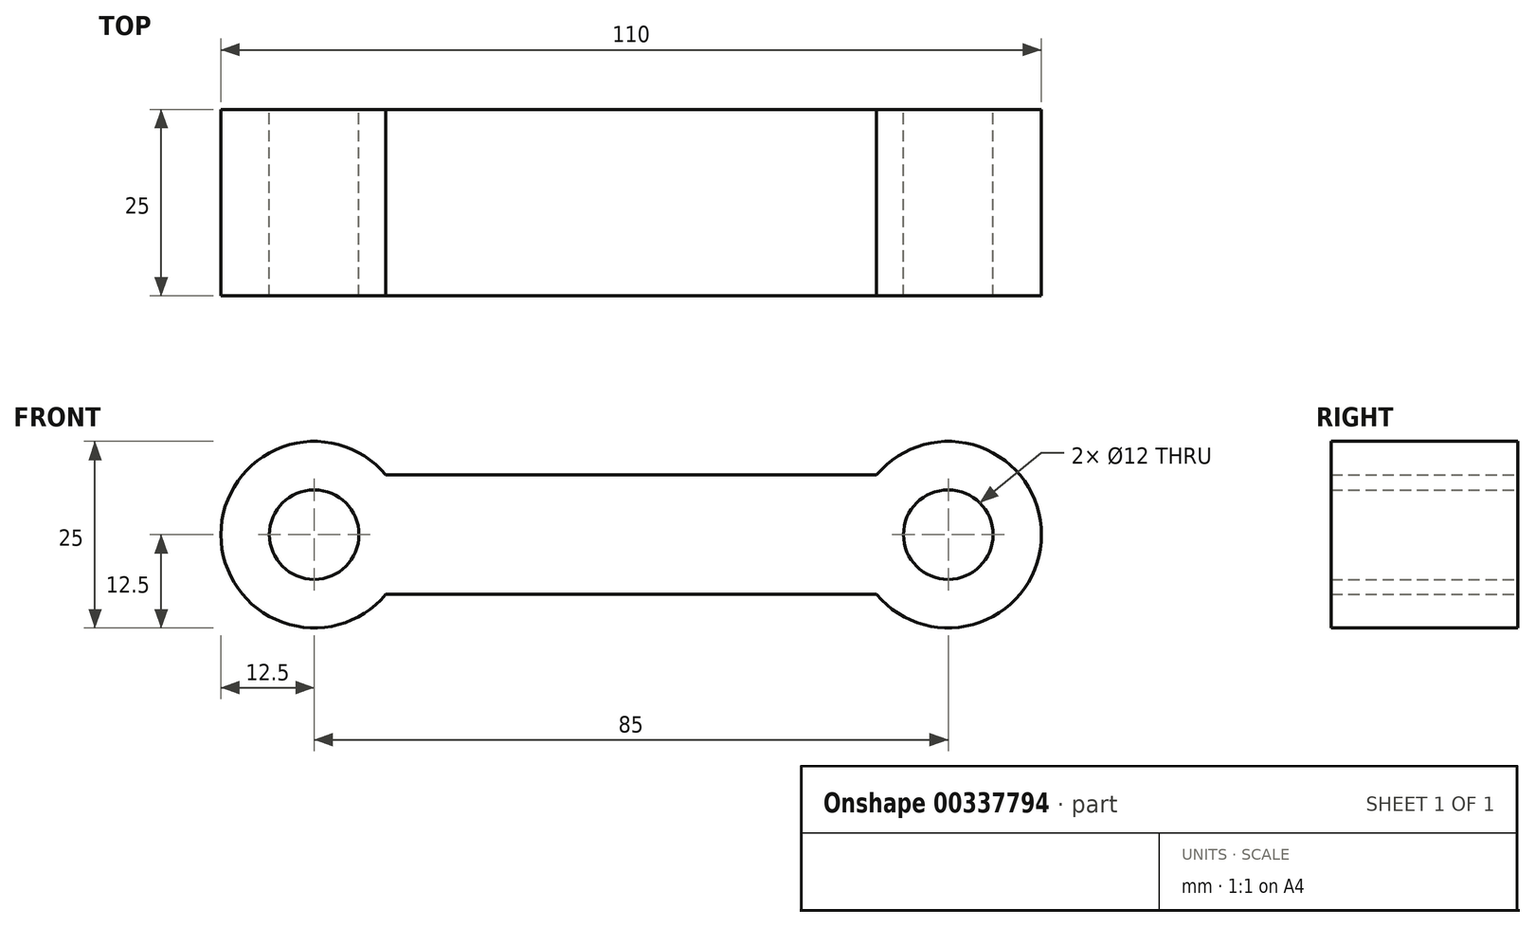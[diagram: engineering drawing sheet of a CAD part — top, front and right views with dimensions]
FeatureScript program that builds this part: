
annotation { "Feature Type Name" : "Feature", "Feature Type Description" : "" }
export const myFeature = defineFeature(function(context is Context, id is Id, definition is map)
    precondition{}
    {
        {
            var Q0;
            Q0=qCreatedBy(makeId("Front.planeOp"),FACE);
            var sketch = newSketch(context, id + "F0", { "sketchPlane" : qUnion([Q0])});
            skCircle(sketch, "E0", {"center": v(0, 0) * mm, "radius": 12.5 * mm});
            skCircle(sketch, "E1", {"center": v(85, 0) * mm, "radius": 12.5 * mm});
            skLineSegment(sketch, "E2", {"start": v(9.6, 8) * mm, "end": v(75.4, 8) * mm});
            skLineSegment(sketch, "E3", {"start": v(0, 0) * mm, "end": v(85, 0) * mm, "construction": true});
            skLineSegment(sketch, "E4.MirrorCS", {"start": v(9.6, -8) * mm, "end": v(75.4, -8) * mm});
            skCircle(sketch, "E5", {"center": v(0, 0) * mm, "radius": 6 * mm});
            skCircle(sketch, "E6", {"center": v(85, 0) * mm, "radius": 6 * mm});
            skSolve(sketch);
        }
        {
            var Q0;
            Q0 = qSketchRegion(id + "F0", true);
            extrude(context, id + "F1", {"entities" : qUnion([Q0]), "depth" : 25 * mm});
        }
    });
